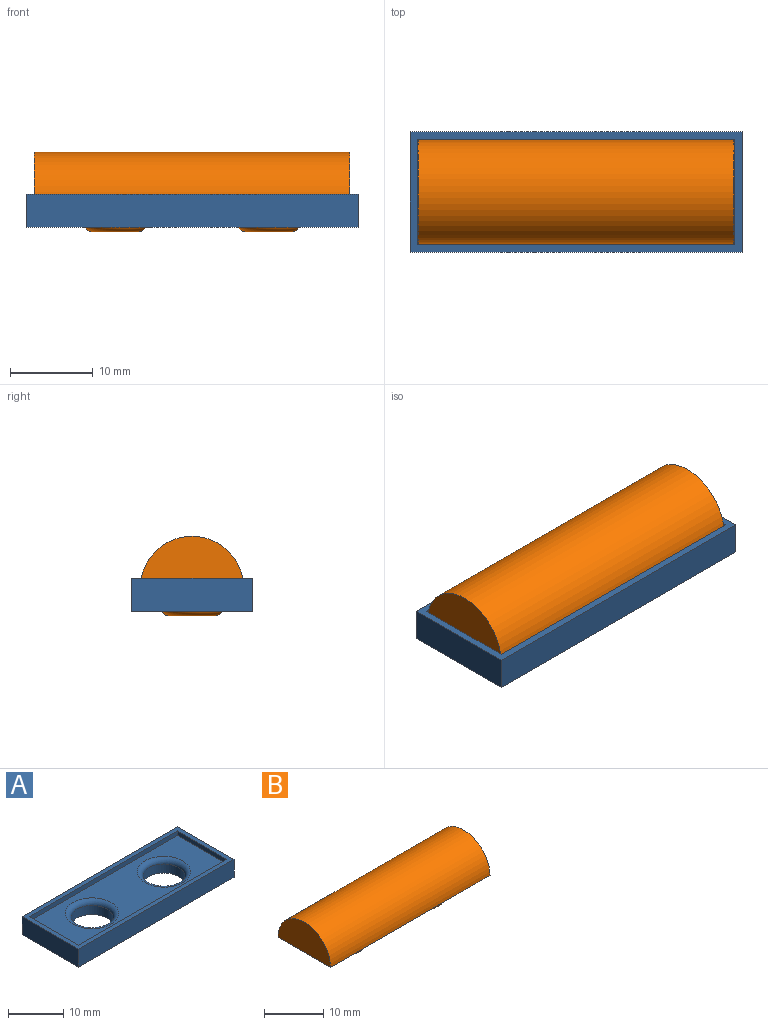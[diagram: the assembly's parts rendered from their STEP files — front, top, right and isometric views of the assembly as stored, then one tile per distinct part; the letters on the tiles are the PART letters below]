
ASSEMBLY  parts=2 mates=1
PART A: 15 faces, bbox 40x14.5x4 mm
  f0: plane 14.5x4mm, normal (1,0,0), area 58mm2, adj f1,f3,f4,f9
  f1: plane 40x4mm, normal (0,-1,0), area 160mm2, adj f0,f2,f4,f9
  f2: plane 14.5x4mm, normal (-1,0,0), area 58mm2, adj f1,f3,f4,f9
  f3: plane 40x4mm, normal (0,1,0), area 160mm2, adj f0,f2,f4,f9
  f4: plane 40x14.5mm, normal (0,0,-1), area 486.9mm2, adj f0,f1,f2,f3,f11,f12
  f5: plane 38.2x1mm, normal (0,1,0), area 38.2mm2, adj f6,f8,f9,f10
  f6: plane 12.7x1mm, normal (-1,0,0), area 12.7mm2, adj f5,f7,f9,f10
  f7: plane 38.2x1mm, normal (0,-1,0), area 38.2mm2, adj f6,f8,f9,f10
  f8: plane 12.7x1mm, normal (1,0,0), area 12.7mm2, adj f5,f7,f9,f10
  f9: plane 40x14.5mm, normal (0,0,1), area 94.9mm2, adj f0,f1,f2,f3,f5,f6,f7,f8
  f10: plane 38.2x12.7mm, normal (0,0,1), area 337.3mm2, adj f5,f6,f7,f8,f13,f14
  f11: cylinder r=3.85mm len=7.7mm, axis (0,0,-1), area 48.4mm2, adj f4,f13
  f12: cylinder r=3.85mm len=7.7mm, axis (0,0,-1), area 48.4mm2, adj f4,f14
  f13: torus R=4.85mm, axis (0,0,-1), area 41.6mm2, adj f10,f11
  f14: torus R=4.85mm, axis (0,0,-1), area 41.6mm2, adj f10,f12
PART B: 10 faces, bbox 38x12.5x9.6 mm
  f0: plane 12.5x6.25mm, normal (-1,0,0), area 61.4mm2, adj f2,f3
  f1: plane 12.5x6.25mm, normal (1,0,0), area 61.4mm2, adj f2,f3
  f2: plane 38x12.5mm, normal (0,0,-1), area 386.6mm2, adj f0,f1,f3,f4,f6
  f3: cylinder r=6.25mm len=38mm, axis (-1,0,0), area 746.1mm2, adj f0,f1,f2
  f4: cylinder r=3.75mm len=7.5mm, axis (0,0,1), area 54.2mm2, adj f2,f9
  f5: plane 5.5x5.5mm, normal (0,0,-1), area 23.8mm2, adj f9
  f6: cylinder r=3.75mm len=7.5mm, axis (0,0,1), area 54.2mm2, adj f2,f8
  f7: plane 5.5x5.5mm, normal (0,0,-1), area 23.8mm2, adj f8
  f8: torus R=2.75mm, axis (0,0,-1), area 33.4mm2, adj f6,f7
  f9: torus R=2.75mm, axis (0,0,-1), area 33.4mm2, adj f4,f5
PLACE A t=(0,0,16.3)mm
PLACE B t=(0,0,2.8)mm
MATE slider B.f4 <-> A.f12  axis (0,0,-1) through (-9.25,0,-0.5)mm
